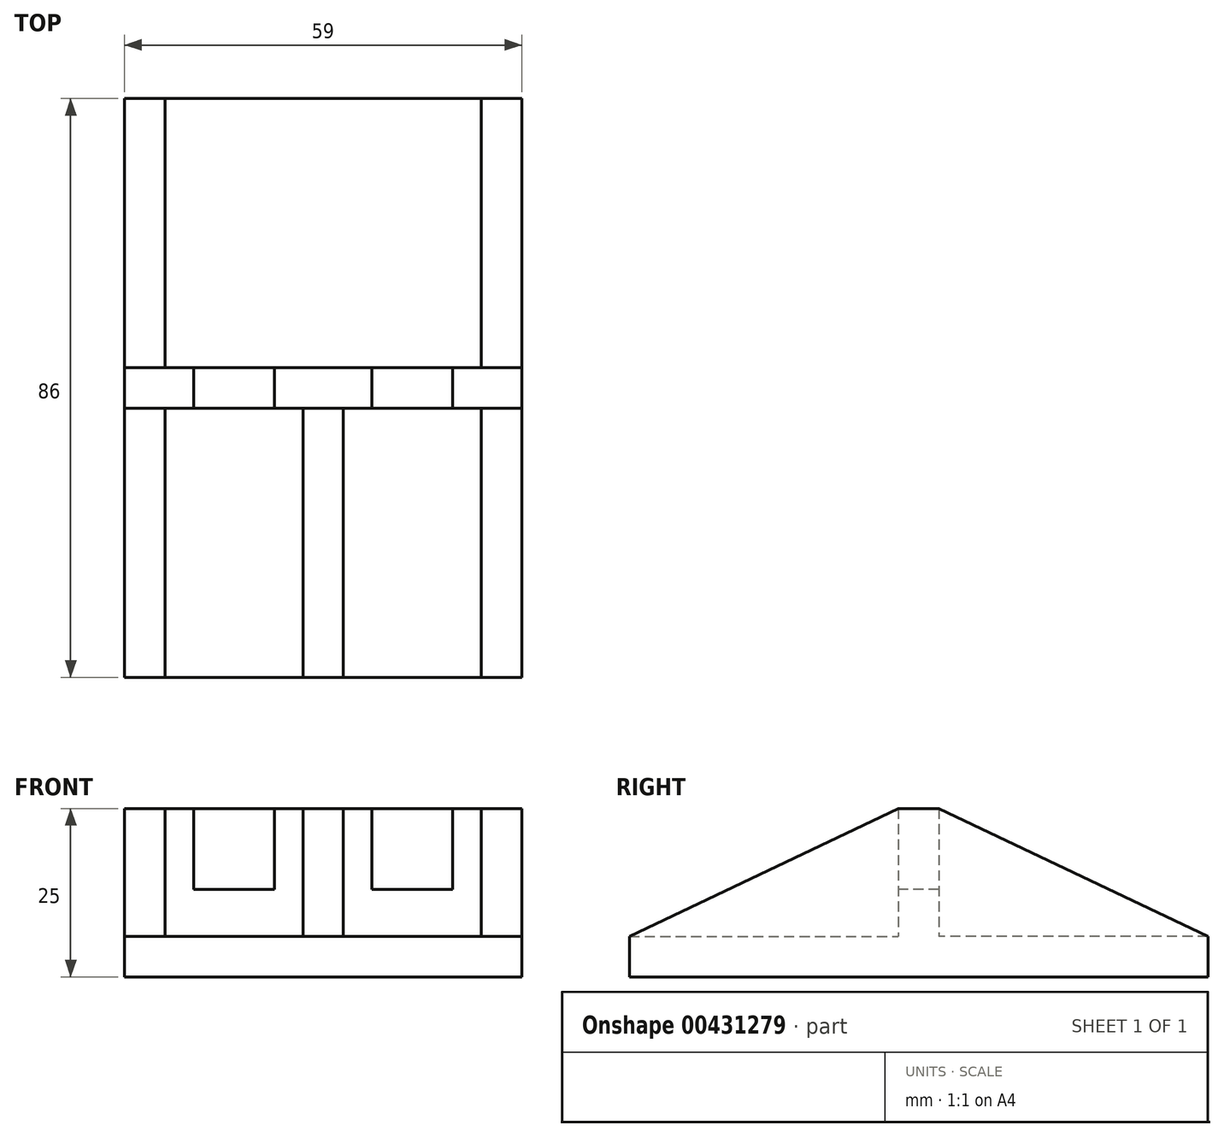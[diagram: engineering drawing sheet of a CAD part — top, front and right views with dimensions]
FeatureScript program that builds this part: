
annotation { "Feature Type Name" : "Feature", "Feature Type Description" : "" }
export const myFeature = defineFeature(function(context is Context, id is Id, definition is map)
    precondition{}
    {
        {
            var Q0;
            Q0=qCreatedBy(makeId("Top.planeOp"),FACE);
            var sketch = newSketch(context, id + "F0", { "sketchPlane" : qUnion([Q0])});
            skLineSegment(sketch, "E0.bottom", {"start": v(-29.5, 43) * mm, "end": v(29.5, 43) * mm});
            skLineSegment(sketch, "E0.top", {"start": v(-29.5, -43) * mm, "end": v(29.5, -43) * mm});
            skLineSegment(sketch, "E0.left", {"start": v(-29.5, 43) * mm, "end": v(-29.5, -43) * mm});
            skLineSegment(sketch, "E0.right", {"start": v(29.5, 43) * mm, "end": v(29.5, -43) * mm});
            skSolve(sketch);
        }
        {
            var Q0;
            Q0=makeQuery(id+"F0.imprint","IMPRINT",FACE,{"disambiguationData":[TD([[makeQuery(id+"F0.imprint","IMPRINT",EDGE,{"derivedFrom":sQuery(id+"F0.wireOp",EDGE,"E0.bottom")}),-1.0]])]});
            extrude(context, id + "F1", {"entities" : qUnion([Q0]), "depth" : 6 * mm});
        }
        {
            var Q0;
            Q0=makeQuery(id+"F1.opExtrude","CAP_FACE",FACE,{"disambiguationData":[OSD([sQuery(id+"F0.wireOp",EDGE,"E0.bottom"),sQuery(id+"F0.wireOp",EDGE,"E0.top"),sQuery(id+"F0.wireOp",EDGE,"E0.left"),sQuery(id+"F0.wireOp",EDGE,"E0.right")])],"isStart":false});
            var sketch = newSketch(context, id + "F2", { "sketchPlane" : qUnion([Q0])});
            skLineSegment(sketch, "E1.bottom", {"start": v(-29.5, 43) * mm, "end": v(-23.5, 43) * mm});
            skLineSegment(sketch, "E1.left", {"start": v(-29.5, 43) * mm, "end": v(-29.5, -43) * mm});
            skLineSegment(sketch, "E1.right", {"start": v(-23.5, 43) * mm, "end": v(-23.5, 3) * mm});
            skLineSegment(sketch, "E2.bottom", {"start": v(-23.5, 3) * mm, "end": v(23.5, 3) * mm});
            skLineSegment(sketch, "E2.top", {"start": v(-23.5, -3) * mm, "end": v(-3, -3) * mm});
            skLineSegment(sketch, "E2.right", {"start": v(29.5, 43) * mm, "end": v(29.5, -43) * mm});
            skLineSegment(sketch, "E3.bottom", {"start": v(-29.5, -43) * mm, "end": v(-23.5, -43) * mm});
            skLineSegment(sketch, "E3.right", {"start": v(-23.5, -43) * mm, "end": v(-23.5, -3) * mm});
            skLineSegment(sketch, "E4.bottom", {"start": v(29.5, -43) * mm, "end": v(23.5, -43) * mm});
            skLineSegment(sketch, "E4.right", {"start": v(23.5, -43) * mm, "end": v(23.5, -3) * mm});
            skLineSegment(sketch, "E5.bottom", {"start": v(29.5, 43) * mm, "end": v(23.5, 43) * mm});
            skLineSegment(sketch, "E5.right", {"start": v(23.5, 43) * mm, "end": v(23.5, 3) * mm});
            skLineSegment(sketch, "E6.bottom", {"start": v(3, -43) * mm, "end": v(-3, -43) * mm});
            skLineSegment(sketch, "E6.left", {"start": v(3, -43) * mm, "end": v(3, -3) * mm});
            skLineSegment(sketch, "E6.right", {"start": v(-3, -43) * mm, "end": v(-3, -3) * mm});
            skLineSegment(sketch, "E7.trimOffspring", {"start": v(3, -3) * mm, "end": v(23.5, -3) * mm});
            skPoint(sketch, "E8.orphan", {"position": v(29.5, -3) * mm});
            skSolve(sketch);
        }
        {
            var Q0;
            Q0=makeQuery(id+"F2.imprint","IMPRINT",FACE,{"disambiguationData":[TD([[makeQuery(id+"F2.imprint","IMPRINT",EDGE,{"derivedFrom":sQuery(id+"F2.wireOp",EDGE,"E1.bottom")}),-1.0]])]});
            extrude(context, id + "F3", {"entities" : qUnion([Q0]), "operationType" : NewBodyOperationType.ADD, "depth" : 19 * mm});
        }
        {
            var Q0;
            Q0=makeQuery(id+"F3.boolean.opBoolean","MERGE",FACE,{"derivedFrom":[makeQuery(id+"F1.opExtrude","SWEPT_FACE",FACE,{"disambiguationData":[OSD([sQuery(id+"F0.wireOp",EDGE,"E0.right")])]}),makeQuery(id+"F3.opExtrude","SWEPT_FACE",FACE,{"disambiguationData":[OSD([sQuery(id+"F2.wireOp",EDGE,"E2.right")])]})]});
            var sketch = newSketch(context, id + "F4", { "sketchPlane" : qUnion([Q0])});
            skLineSegment(sketch, "E9", {"start": v(-43, 6) * mm, "end": v(-3, 25) * mm});
            skLineSegment(sketch, "E10", {"start": v(-3, 25) * mm, "end": v(-43, 25) * mm});
            skLineSegment(sketch, "E11", {"start": v(-43, 25) * mm, "end": v(-43, 6) * mm});
            skLineSegment(sketch, "E12", {"start": v(43, 6) * mm, "end": v(3, 25) * mm});
            skLineSegment(sketch, "E13", {"start": v(3, 25) * mm, "end": v(43, 25) * mm});
            skLineSegment(sketch, "E14", {"start": v(43, 25) * mm, "end": v(43, 6) * mm});
            skSolve(sketch);
        }
        {
            var Q0;
            Q0=makeQuery(id+"F4.imprint","IMPRINT",FACE,{"disambiguationData":[TD([[makeQuery(id+"F4.imprint","IMPRINT",EDGE,{"derivedFrom":sQuery(id+"F4.wireOp",EDGE,"E9")}),1.0]])]});
            var Q1;
            Q1=makeQuery(id+"F4.imprint","IMPRINT",FACE,{"disambiguationData":[TD([[makeQuery(id+"F4.imprint","IMPRINT",EDGE,{"derivedFrom":sQuery(id+"F4.wireOp",EDGE,"E12")}),-1.0]])]});
            extrude(context, id + "F5", {"entities" : qUnion([Q0, Q1]), "operationType" : NewBodyOperationType.REMOVE, "endBound" : BoundingType.THROUGH_ALL, "oppositeDirection" : true, "depth" : 25 * mm});
        }
        {
            var Q0;
            Q0=makeQuery(id+"F3.opExtrude","SWEPT_FACE",FACE,{"disambiguationData":[OSD([sQuery(id+"F2.wireOp",EDGE,"E2.top")])]});
            var sketch = newSketch(context, id + "F6", { "sketchPlane" : qUnion([Q0])});
            skLineSegment(sketch, "E15.bottom", {"start": v(-19.25, 25) * mm, "end": v(-7.25, 25) * mm});
            skLineSegment(sketch, "E15.top", {"start": v(-19.25, 13) * mm, "end": v(-7.25, 13) * mm});
            skLineSegment(sketch, "E15.left", {"start": v(-19.25, 25) * mm, "end": v(-19.25, 13) * mm});
            skLineSegment(sketch, "E15.right", {"start": v(-7.25, 25) * mm, "end": v(-7.25, 13) * mm});
            skLineSegment(sketch, "E16.bottom", {"start": v(7.25, 25) * mm, "end": v(19.25, 25) * mm});
            skLineSegment(sketch, "E16.top", {"start": v(7.25, 13) * mm, "end": v(19.25, 13) * mm});
            skLineSegment(sketch, "E16.left", {"start": v(7.25, 25) * mm, "end": v(7.25, 13) * mm});
            skLineSegment(sketch, "E16.right", {"start": v(19.25, 25) * mm, "end": v(19.25, 13) * mm});
            skSolve(sketch);
        }
        {
            var Q0;
            Q0=makeQuery(id+"F6.imprint","IMPRINT",FACE,{"disambiguationData":[TD([[makeQuery(id+"F6.imprint","IMPRINT",EDGE,{"derivedFrom":sQuery(id+"F6.wireOp",EDGE,"E15.bottom")}),-1.0]])]});
            var Q1;
            Q1=makeQuery(id+"F6.imprint","IMPRINT",FACE,{"disambiguationData":[TD([[makeQuery(id+"F6.imprint","IMPRINT",EDGE,{"derivedFrom":sQuery(id+"F6.wireOp",EDGE,"E16.bottom")}),-1.0]])]});
            extrude(context, id + "F7", {"entities" : qUnion([Q0, Q1]), "oppositeDirection" : true, "depth" : 6 * mm});
        }
    });
